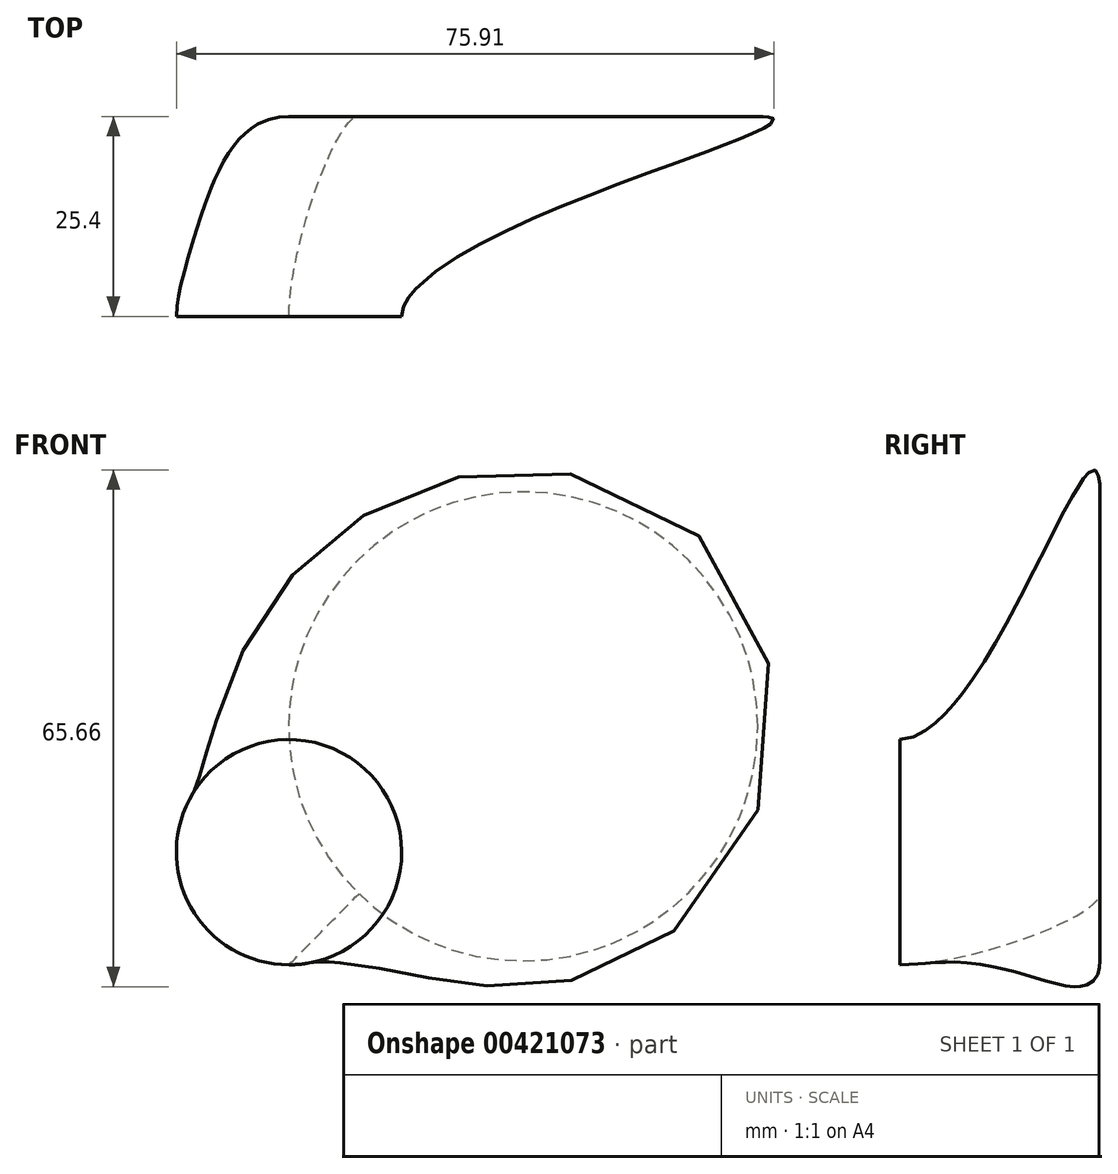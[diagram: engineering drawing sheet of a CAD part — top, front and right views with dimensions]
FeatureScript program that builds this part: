
annotation { "Feature Type Name" : "Feature", "Feature Type Description" : "" }
export const myFeature = defineFeature(function(context is Context, id is Id, definition is map)
    precondition{}
    {
        {
            var Q0;
            Q0=qCreatedBy(makeId("Front.planeOp"),FACE);
            var sketch = newSketch(context, id + "F0", { "sketchPlane" : qUnion([Q0])});
            skCircle(sketch, "E0", {"center": v(-63.8, 59.13) * mm, "radius": 29.79 * mm});
            skSolve(sketch);
        }
        {
            var Q0;
            Q0=makeQuery(id+"F0.imprint","IMPRINT",FACE,{"disambiguationData":[TD([[makeQuery(id+"F0.imprint","IMPRINT",EDGE,{"derivedFrom":sQuery(id+"F0.wireOp",EDGE,"E0")}),1.0]])]});
            cPlane(context, id + "F1", {"entities" : qUnion([Q0]), "cplaneType" : CPlaneType.OFFSET, "offset" : 25.4 * mm, "width" : 152.4 * mm, "height" : 152.4 * mm});
        }
        {
            var Q0;
            Q0=qCreatedBy(id+"F1.planeOp",FACE);
            var sketch = newSketch(context, id + "F2", { "sketchPlane" : qUnion([Q0])});
            skCircle(sketch, "E1", {"center": v(-93.55, 43.15) * mm, "radius": 14.3 * mm});
            skSolve(sketch);
        }
        {
            var Q0;
            Q0=makeQuery(id+"F2.imprint","IMPRINT",FACE,{"disambiguationData":[TD([[makeQuery(id+"F2.imprint","IMPRINT",EDGE,{"derivedFrom":sQuery(id+"F2.wireOp",EDGE,"E1")}),1.0]])]});
            var Q1;
            Q1=makeQuery(id+"F0.imprint","IMPRINT",FACE,{"disambiguationData":[TD([[makeQuery(id+"F0.imprint","IMPRINT",EDGE,{"derivedFrom":sQuery(id+"F0.wireOp",EDGE,"E0")}),1.0]])]});
            loft(context, id + "F3", {"startCondition" : LoftEndDerivativeType.NORMAL_TO_PROFILE, "startMagnitude" : 1, "endCondition" : LoftEndDerivativeType.TANGENT_TO_PROFILE, "endMagnitude" : 1, "sheetProfilesArray" : [{ "sheetProfileEntities" : qUnion([Q0]) }, { "sheetProfileEntities" : qUnion([Q1]) }]});
        }
    });
